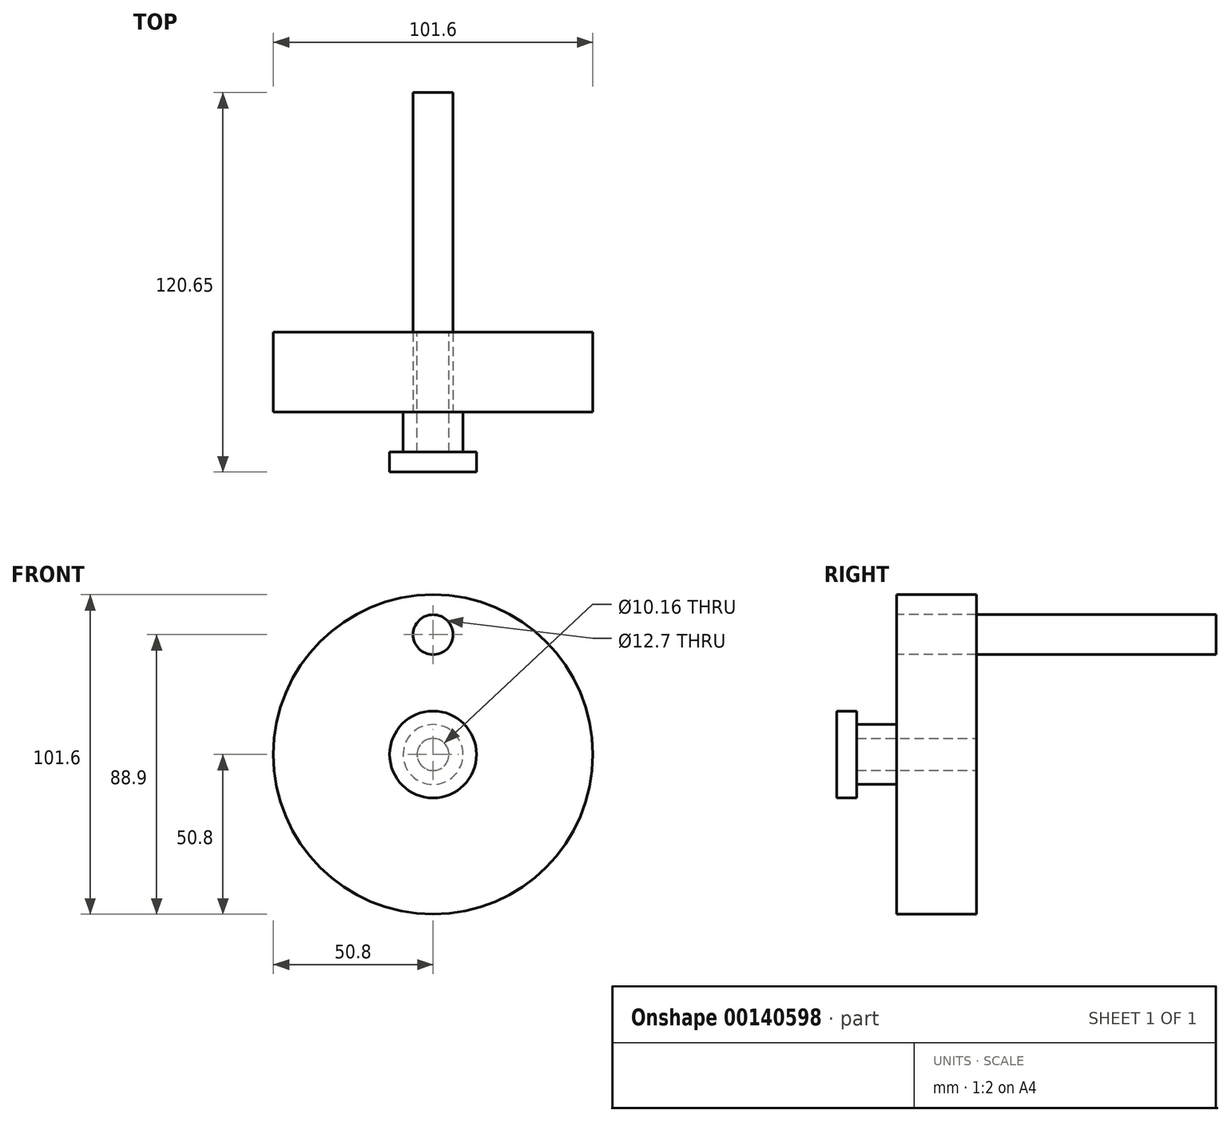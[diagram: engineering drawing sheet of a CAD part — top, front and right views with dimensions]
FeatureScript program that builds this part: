
annotation { "Feature Type Name" : "Feature", "Feature Type Description" : "" }
export const myFeature = defineFeature(function(context is Context, id is Id, definition is map)
    precondition{}
    {
        {
            var Q0;
            Q0=qCreatedBy(makeId("Front.planeOp"),FACE);
            var sketch = newSketch(context, id + "F0", { "sketchPlane" : qUnion([Q0])});
            skCircle(sketch, "E0", {"center": v(0, 0) * mm, "radius": 50.8 * mm});
            skCircle(sketch, "E1", {"center": v(0, 0) * mm, "radius": 25.4 * mm, "construction": true});
            skCircle(sketch, "E2", {"center": v(0, 25.4) * mm, "radius": 3.81 * mm, "construction": true});
            skSolve(sketch);
        }
        {
            var Q0;
            Q0=qSketchRegion(id+"F0",true);
            extrude(context, id + "F1", {"entities" : qUnion([Q0]), "depth" : 25.4 * mm});
        }
        {
            var Q0;
            Q0=makeQuery(id+"F1.opExtrude","CAP_FACE",FACE,{"disambiguationData":[OSD([sQuery(id+"F0.wireOp",EDGE,"E0")])],"isStart":false});
            var sketch = newSketch(context, id + "F2", { "sketchPlane" : qUnion([Q0])});
            skCircle(sketch, "E3", {"center": v(0, 0) * mm, "radius": 9.53 * mm});
            skSolve(sketch);
        }
        {
            var Q0;
            Q0=qSketchRegion(id+"F2",true);
            extrude(context, id + "F3", {"entities" : qUnion([Q0]), "operationType" : NewBodyOperationType.ADD, "depth" : 12.7 * mm});
        }
        {
            var Q0;
            Q0=makeQuery(id+"F1.opExtrude","CAP_FACE",FACE,{"disambiguationData":[OSD([sQuery(id+"F0.wireOp",EDGE,"E0")])],"isStart":true});
            var sketch = newSketch(context, id + "F4", { "sketchPlane" : qUnion([Q0])});
            skCircle(sketch, "E4", {"center": v(0, 0) * mm, "radius": 5.08 * mm});
            skSolve(sketch);
        }
        {
            var Q0;
            Q0=qSketchRegion(id+"F4",true);
            extrude(context, id + "F5", {"entities" : qUnion([Q0]), "operationType" : NewBodyOperationType.REMOVE, "oppositeDirection" : true, "depth" : 50.8 * mm});
        }
        {
            var Q0;
            Q0=makeQuery(id+"F1.opExtrude","CAP_FACE",FACE,{"disambiguationData":[OSD([sQuery(id+"F0.wireOp",EDGE,"E0")])],"isStart":false});
            var sketch = newSketch(context, id + "F6", { "sketchPlane" : qUnion([Q0])});
            skCircle(sketch, "E5", {"center": v(0, 38.1) * mm, "radius": 6.35 * mm});
            skSolve(sketch);
        }
        {
            var Q0;
            Q0=qSketchRegion(id+"F6",true);
            extrude(context, id + "F7", {"entities" : qUnion([Q0]), "operationType" : NewBodyOperationType.REMOVE, "oppositeDirection" : true, "depth" : 25.4 * mm});
        }
        {
            var Q0;
            Q0=qSketchRegion(id+"F6",true);
            extrude(context, id + "F8", {"entities" : qUnion([Q0]), "oppositeDirection" : true, "depth" : 101.6 * mm});
        }
        {
            var Q0;
            Q0=makeQuery(id+"F3.opExtrude","CAP_FACE",FACE,{"disambiguationData":[OSD([sQuery(id+"F2.wireOp",EDGE,"E3")])],"isStart":false});
            var sketch = newSketch(context, id + "F9", { "sketchPlane" : qUnion([Q0])});
            skCircle(sketch, "E6", {"center": v(0, 0) * mm, "radius": 13.81 * mm});
            skSolve(sketch);
        }
        {
            var Q0;
            Q0=qSketchRegion(id+"F9",true);
            extrude(context, id + "F10", {"entities" : qUnion([Q0]), "depth" : 6.35 * mm});
        }
    });
